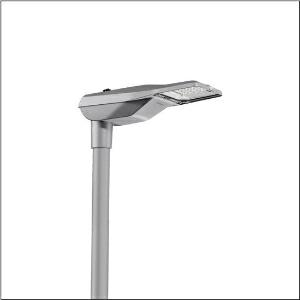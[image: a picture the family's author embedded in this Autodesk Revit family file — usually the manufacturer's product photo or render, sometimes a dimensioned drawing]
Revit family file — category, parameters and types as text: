
# Revit family: streetlight_sl_21_micro___st1_0ab_5xe1m33s08db_765d
name_source: partatom
category: Lighting Fixtures
units: mm (PartAtom-declared; Revit-internal decimal feet)

## family parameters
Cut with Voids When Loaded = No
Host = Face
Light Source = No
Part Type = Normal
Room Calculation Point = No
Round Connector Dimension = Use Diameter
Shared = No

## types (1)
- --- (1 x LED, 4500 lm, 39.1 W, 3000K)
    Apparent Load = 39 VA
    CIE Flux Codes = 38 73 97 100 100
    Color Rendering = 70
    Color Temperature = 3000K
    Default Elevation = 1800 mm
    Description = Streetlight SL 21 micro, mast luminaire, primary light control with lens, of PMMA, primary optical cover: cover, of toughened safety glass, transparent, light distribution: ST1.0aB, light emission: direct distribution, primary light characteristic: asymmetric, installation type: side-entry, post-top, LED, High Power LED, rated luminous flux: 4.500lm, luminous efficacy: 115lm/W, light colour: 730, colour temperature: 3000K, control: flexible luminous flux parameterisation, time-dependent luminous flux control, constant luminous flux control, overheat protection, presetting dimming logarithmic, mains connection: 220..240V, AC, 50/60Hz, start of lifetime: 39W, end of service life: 41W, reduction: 18W, luminaire housing, of diecast aluminium, powder-coated, Siteco® metallic grey (DB 702S), corrosivity category C5 mid according to DIN EN ISO 12944, please order mast flange separately, inclination adjustable: 0°, 5°, 10°, 15°, sealing non-destructively replaceable, multi-level sealing system, length: 528mm, width: 235mm, height: 110mm, mast flange for spigot size: 42mm (side-entry): 5XC10008XM4, 60/48mm (side-entry/post-top): 5XC10108XM2, 76/60mm (side-entry/post-top): 5XC10108XM1, Smart Interface above, protection rating (complete): IP66, insulation class (complete): insulation class II (safety insulation), certification: CE, ENEC, ENEC+, VDE, impact resistance: IK09, permissible operating ambient temperature for outdoor applications: -40..+50°C, standard-compliant lighting for roads and squares, packaging unit: 1 piece

Light Distribution: ST1.0aB
    Height = 110 mm
    Lamp = 1 x LED
    Lamp Light Flux = 4500 lm
    Lamp Power = 39.1 W
    Lamp count = 1
    Length = 528 mm
    Luminous efficacy = 115 lm/W
    Manufacturer = Siteco
    ModVariant = No
    Model = 5XE1M33S08DB
    Number of Poles = 1
    OnlyDefault = Yes
    Power Factor = 1
    Product Name = Streetlight SL 21 micro | ST1.0aB
    Product group = mast luminaire | pylon top
    ProductGroupID = 6100
    Protection Class = Protection class II
    Protection Degree = IP 66
    RLX_Detail_Level = 1
    RLX_Emergency_Light_Flux = 0 lm
    RLX_Emergency_Type = 0
    RLX_Emergency_Type_DB = No
    RlxData = <blob elided: 98353 chars, md5=b7c8dc4c>
    Socket = socket
    Standby Power = 0 W
    System Light Flux = 4500 lm
    System Power = 39 W
    Type Comments = factory setting: luminous flux: 100 % | dim-lin: 254 | 765 mA
    Type Image = l_1277292.jpg
    URL = http://relux.com
    VarID = @adj_086281
    Voltage = 0 V
    Weight = 0.00 kg
    Width = 235 mm

## geometry (parser evidence)
native form markers: Blend x4, Sweep x9
no freeform markers — native parametric forms only
